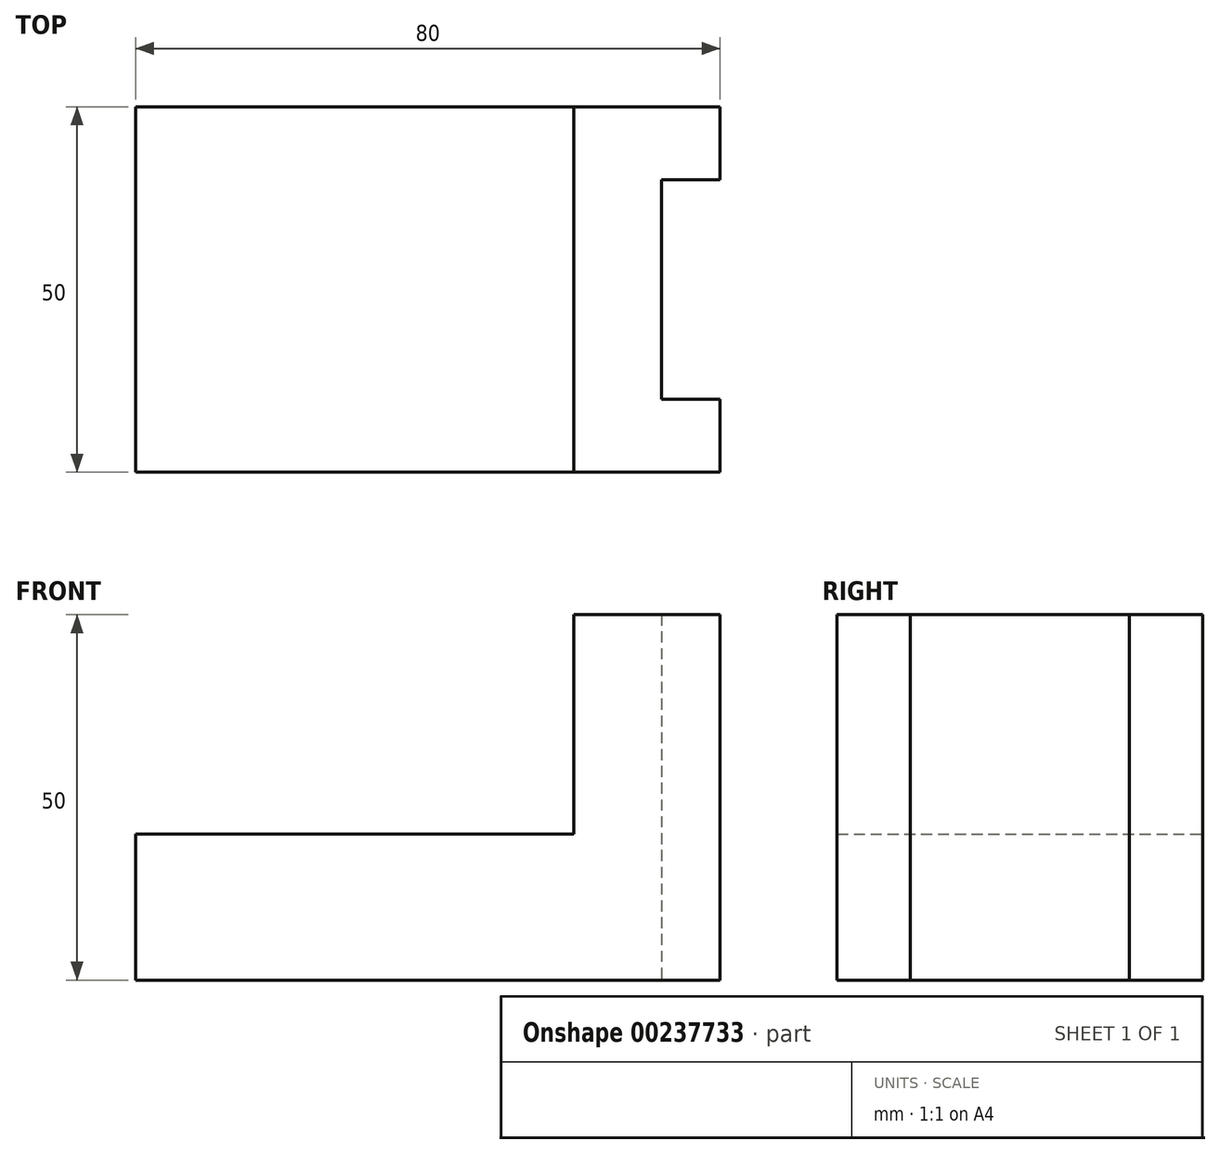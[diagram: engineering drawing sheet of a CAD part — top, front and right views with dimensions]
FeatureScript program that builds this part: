
annotation { "Feature Type Name" : "Feature", "Feature Type Description" : "" }
export const myFeature = defineFeature(function(context is Context, id is Id, definition is map)
    precondition{}
    {
        {
            var Q0;
            Q0=qCreatedBy(makeId("Top.planeOp"),FACE);
            var sketch = newSketch(context, id + "F0", { "sketchPlane" : qUnion([Q0])});
            skLineSegment(sketch, "E0.bottom", {"start": v(0, 0) * mm, "end": v(-60, 0) * mm});
            skLineSegment(sketch, "E0.top", {"start": v(0, 50) * mm, "end": v(-60, 50) * mm});
            skLineSegment(sketch, "E0.left", {"start": v(0, 0) * mm, "end": v(0, 50) * mm});
            skLineSegment(sketch, "E0.right", {"start": v(-60, 0) * mm, "end": v(-60, 50) * mm});
            skLineSegment(sketch, "E1.bottom", {"start": v(0, 0) * mm, "end": v(20, 0) * mm});
            skLineSegment(sketch, "E1.top", {"start": v(0, 50) * mm, "end": v(20, 50) * mm});
            skLineSegment(sketch, "E1.right", {"start": v(20, 0) * mm, "end": v(20, 50) * mm});
            skLineSegment(sketch, "E2.bottom", {"start": v(20, 40) * mm, "end": v(12, 40) * mm});
            skLineSegment(sketch, "E2.top", {"start": v(20, 10) * mm, "end": v(12, 10) * mm});
            skLineSegment(sketch, "E2.left", {"start": v(20, 40) * mm, "end": v(20, 10) * mm});
            skLineSegment(sketch, "E2.right", {"start": v(12, 40) * mm, "end": v(12, 10) * mm});
            skSolve(sketch);
        }
        {
            var Q0;
            Q0=makeQuery(id+"F0.imprint","IMPRINT",FACE,{"disambiguationData":[TD([[makeQuery(id+"F0.imprint","IMPRINT",EDGE,{"derivedFrom":sQuery(id+"F0.wireOp",EDGE,"E0.bottom")}),-1.0]])]});
            extrude(context, id + "F1", {"entities" : qUnion([Q0]), "depth" : 20 * mm});
        }
        {
            var Q0;
            {var subQ1=sQuery(id+"F0.wireOp",EDGE,"E1.bottom");Q0=makeQuery(id+"F0.imprint","IMPRINT",FACE,{"disambiguationData":[TD([[makeQuery(id+"F0.imprint","IMPRINT",EDGE,{"derivedFrom":subQ1}),1.0]])]});}
            extrude(context, id + "F2", {"entities" : qUnion([Q0]), "operationType" : NewBodyOperationType.ADD, "depth" : 50 * mm});
        }
    });
